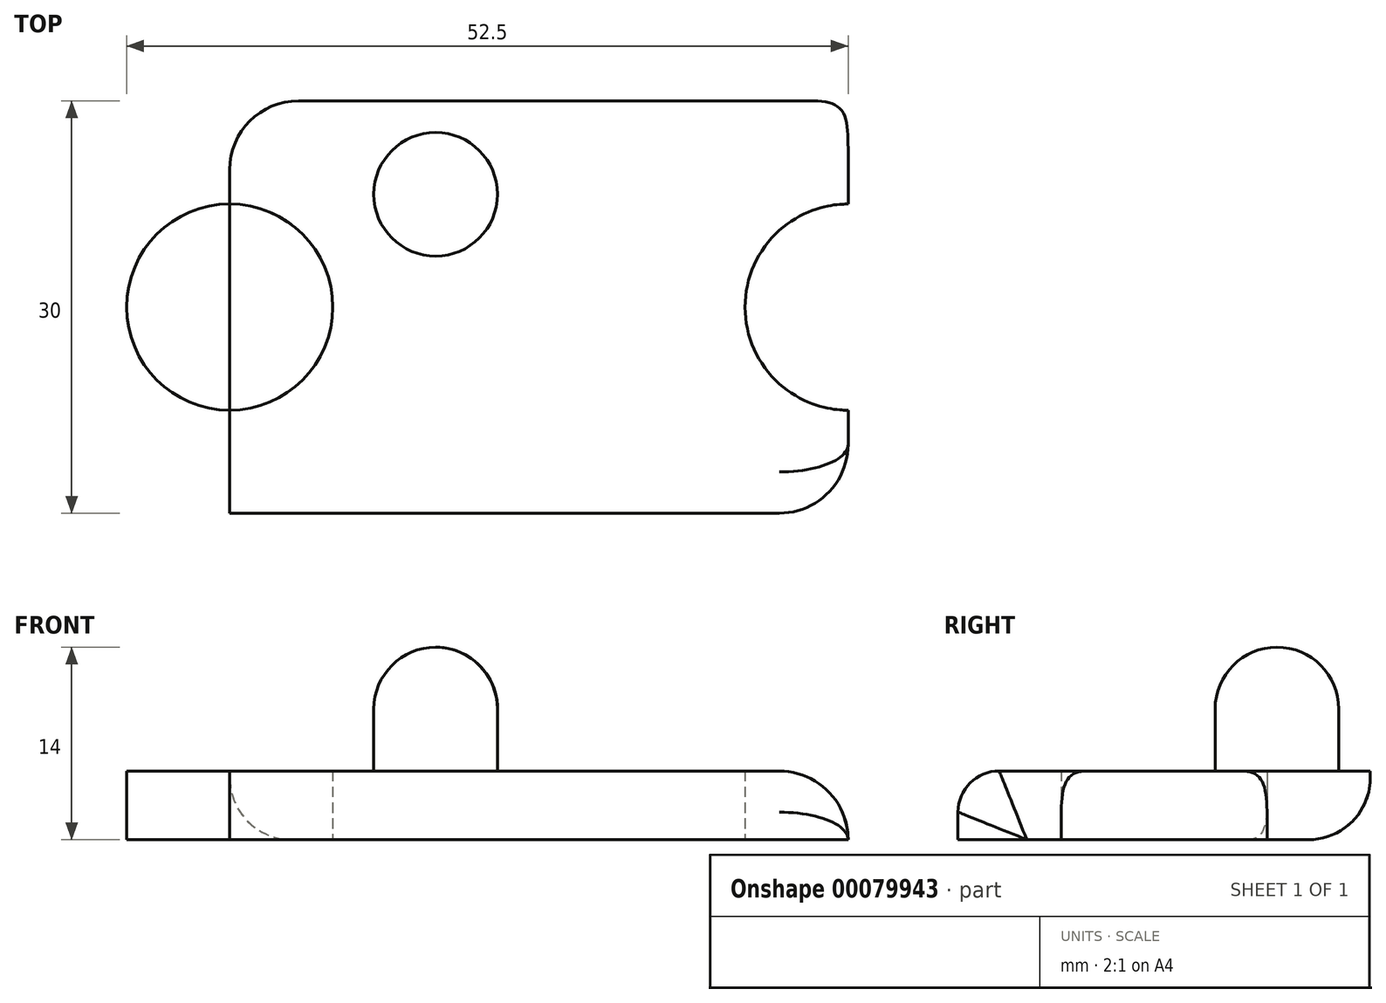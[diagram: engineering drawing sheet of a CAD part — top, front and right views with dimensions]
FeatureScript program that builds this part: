
annotation { "Feature Type Name" : "Feature", "Feature Type Description" : "" }
export const myFeature = defineFeature(function(context is Context, id is Id, definition is map)
    precondition{}
    {
        {
            var Q0;
            Q0=qCreatedBy(makeId("Top.planeOp"),FACE);
            var sketch = newSketch(context, id + "F0", { "sketchPlane" : qUnion([Q0])});
            skLineSegment(sketch, "E0.bottom", {"start": v(22.5, 15) * mm, "end": v(-22.5, 15) * mm});
            skLineSegment(sketch, "E0.top", {"start": v(22.5, -15) * mm, "end": v(-22.5, -15) * mm});
            skLineSegment(sketch, "E0.left", {"start": v(22.5, 15) * mm, "end": v(22.5, -15) * mm});
            skLineSegment(sketch, "E0.right", {"start": v(-22.5, 15) * mm, "end": v(-22.5, -15) * mm});
            skPoint(sketch, "E0.middle", {"position": v(0, 0) * mm});
            skCircle(sketch, "E1", {"center": v(-22.5, 0) * mm, "radius": 7.5 * mm});
            skLineSegment(sketch, "E2", {"start": v(-14.09, 22.41) * mm, "end": v(45.91, 22.41) * mm, "construction": true});
            skLineSegment(sketch, "E3", {"start": v(45.91, 22.41) * mm, "end": v(58.22, 13.84) * mm, "construction": true});
            skLineSegment(sketch, "E4", {"start": v(0, 15) * mm, "end": v(0, -15) * mm, "construction": true});
            skCircle(sketch, "E5.MirrorC", {"center": v(22.5, 0) * mm, "radius": 7.5 * mm});
            skSolve(sketch);
        }
        {
            var Q0;
            {var subQ4=sQuery(id+"F0.wireOp",EDGE,"E0.bottom");Q0=makeQuery(id+"F0.imprint","IMPRINT",FACE,{"disambiguationData":[TD([[makeQuery(id+"F0.imprint","IMPRINT",EDGE,{"derivedFrom":subQ4}),1.0]])]});}
            var Q1;
            {var subQ0=sQuery(id+"F0.wireOp",EDGE,"E1");var subQ1=sQuery(id+"F0.wireOp",EDGE,"E0.right");var subQ2=makeQuery(id+"F0.imprint","INTERSECT",VERTEX,{"disambiguationData":[OD(0.0)],"derivedFrom":[subQ1,subQ0]});Q1=makeQuery(id+"F0.imprint","IMPRINT",FACE,{"disambiguationData":[TD([[makeQuery(id+"F0.imprint","IMPRINT",EDGE,{"disambiguationData":[TD([[subQ2,-1.0]])],"derivedFrom":subQ1}),-1.0]])]});}
            extrude(context, id + "F1", {"entities" : qUnion([Q0, Q1]), "depth" : 5 * mm});
        }
        {
            var Q0;
            Q0=makeQuery(id+"F1.opExtrude","CAP_EDGE",EDGE,{"disambiguationData":[OSD([sQuery(id+"F0.wireOp",EDGE,"E0.top")])],"isStart":false});
            fillet(context, id + "F2", {"entities" : qUnion([Q0]), "radius" : 3 * mm, "tangentPropagation" : true, "allowEdgeOverflow" : false});
        }
        {
            var Q0;
            {var subQ0=sQuery(id+"F0.wireOp",EDGE,"E0.left");var subQ1=sQuery(id+"F0.wireOp",EDGE,"E0.top");Q0=makeQuery(id+"F2.opFillet","BLEND_EDGE",EDGE,{"blendedFrom":[makeQuery(id+"F1.opExtrude","CAP_EDGE",EDGE,{"disambiguationData":[OSD([subQ1])],"isStart":false}),makeQuery(id+"F1.opExtrude","SWEPT_FACE",FACE,{"disambiguationData":[OSD([subQ0]),TDD([makeQuery(id+"F0.imprint","IMPRINT",EDGE,{"disambiguationData":[TD([[makeQuery(id+"F0.imprint","INTERSECT",VERTEX,{"derivedFrom":[subQ1,subQ0]}),1.0]])],"derivedFrom":subQ0})])]})],"blendedInto":[makeQuery(id+"F1.opExtrude","SWEPT_FACE",FACE,{"disambiguationData":[OSD([subQ0]),TDD([makeQuery(id+"F0.imprint","IMPRINT",EDGE,{"disambiguationData":[TD([[makeQuery(id+"F0.imprint","INTERSECT",VERTEX,{"derivedFrom":[subQ1,subQ0]}),1.0]])],"derivedFrom":subQ0})])]})]});}
            var Q1;
            {var subQ0=sQuery(id+"F0.wireOp",EDGE,"E0.left");Q1=makeQuery(id+"F1.opExtrude","CAP_EDGE",EDGE,{"disambiguationData":[OSD([subQ0]),TDD([makeQuery(id+"F0.imprint","IMPRINT",EDGE,{"disambiguationData":[TD([[makeQuery(id+"F0.imprint","INTERSECT",VERTEX,{"derivedFrom":[sQuery(id+"F0.wireOp",EDGE,"E0.bottom"),subQ0]}),-1.0]])],"derivedFrom":subQ0})])],"isStart":false});}
            fillet(context, id + "F3", {"entities" : qUnion([Q0, Q1]), "radius" : 5 * mm, "tangentPropagation" : true, "allowEdgeOverflow" : false});
        }
        {
            var Q0;
            Q0=makeQuery(id+"F1.opExtrude","SWEPT_EDGE",EDGE,{"disambiguationData":[OSD([sQuery(id+"F0.wireOp",EDGE,"E0.bottom"),sQuery(id+"F0.wireOp",EDGE,"E0.right")])]});
            fillet(context, id + "F4", {"entities" : qUnion([Q0]), "radius" : 5 * mm, "tangentPropagation" : true, "allowEdgeOverflow" : false});
        }
        {
            var Q0;
            Q0=makeQuery(id+"F1.opExtrude","CAP_FACE",FACE,{"disambiguationData":[OSD([sQuery(id+"F0.wireOp",EDGE,"E0.bottom"),sQuery(id+"F0.wireOp",EDGE,"E0.top"),sQuery(id+"F0.wireOp",EDGE,"E0.left"),sQuery(id+"F0.wireOp",EDGE,"E0.right"),sQuery(id+"F0.wireOp",EDGE,"E1"),sQuery(id+"F0.wireOp",EDGE,"E5.MirrorC")])],"isStart":false});
            var sketch = newSketch(context, id + "F5", { "sketchPlane" : qUnion([Q0])});
            skCircle(sketch, "E6", {"center": v(-7.52, 8.2) * mm, "radius": 4.5 * mm});
            skLineSegment(sketch, "E7", {"start": v(-22.5, 7.5) * mm, "end": v(-7.52, 8.2) * mm, "construction": true});
            skSolve(sketch);
        }
        {
            var Q0;
            Q0=makeQuery(id+"F5.imprint","IMPRINT",FACE,{"disambiguationData":[TD([[makeQuery(id+"F5.imprint","IMPRINT",EDGE,{"derivedFrom":sQuery(id+"F5.wireOp",EDGE,"E6")}),1.0]])]});
            extrude(context, id + "F6", {"entities" : qUnion([Q0]), "operationType" : NewBodyOperationType.ADD, "depth" : 9 * mm});
        }
        {
            var Q0;
            Q0=makeQuery(id+"F6.opExtrude","CAP_EDGE",EDGE,{"disambiguationData":[OSD([sQuery(id+"F5.wireOp",EDGE,"E6")])],"isStart":false});
            var Q1;
            Q1=makeQuery(id+"F1.opExtrude","CAP_EDGE",EDGE,{"disambiguationData":[OSD([sQuery(id+"F0.wireOp",EDGE,"E0.bottom")])],"isStart":true});
            var Q2;
            Q2=makeQuery(id+"F6.opExtrude","CAP_EDGE",EDGE,{"disambiguationData":[OSD([sQuery(id+"F5.wireOp",EDGE,"E6")])],"isStart":true});
            fillet(context, id + "F7", {"entities" : qUnion([Q0, Q1, Q2]), "radius" : 4.5 * mm, "tangentPropagation" : true, "allowEdgeOverflow" : false});
        }
    });
